# Revit family: RN 22120 Valvola inclinata
name_source: partatom
category: Rohrzubehör
units: mm (PartAtom-declared; Revit-internal decimal feet)

## family parameters
Arbeitsebenenbasiert = Nein
Beim Laden mit Abzugskörper schneiden = Nein
Bemaßung runder Anschluss = Durchmesser verwenden
Gemeinsam genutzt = Nein
Immer vertikal = Ja
Teiletyp = Ventil - Zerlegung in

## types (7) — shared parameters
1.010.00.2 Blattnummer der Richtlinie = 17
1.010.00.3 Ausgabedatum (Monat) der Richtlinie = 201601
1.010.00.4 Herstellername = R. Nussbaum AG
1.010.00.5 Revisionsdatum der Datei = 20190528
1.010.00.6 Webadresse des Herstellers = http://www.nussbaum.ch
1.100.00.3 Sortiernummer für Anzeigereihenfolge = 1
1.100.00.4 Produktbezeichnung = Absperrarmaturen
1.960/3L.00.8 Link (URL) = https://www.nussbaum.ch
17.700.00.4 Armaturentyp = 1
17.700.00.7 Maximale Betriebstemperatur TB [°C] = 90
17.700.00.8 Maximaler Betriebsdruck (Arbeitsdruck) ps [1.0 · 105 Pa] = 16
Connector Visibility = Nein
EnclosingSpace Visibility = Nein
Hersteller = R. Nussbauzm AG
URL = https://www.nussbaum.ch

## per-type parameters (varying)
- DN 25: 1.800.00.3 TGA-Nummer=001059???00000000000000000000200700000000000000001???00000; 1.810.00.3 Hersteller-Bestellnummer=22120.23; 1.810.00.4 DATANORM-Nummer=22120.23; 1.810.00.5 StLB-Nummer=727.113; 1.810.00.6 GTIN-Nummer=7612945733429; 17.700.00.30 Produktbeschreibung=22120.23, Schrägsitzventil, mit Flanschen, DN=25; 17.700.00.5 Nennweite DN=25; 17.700.00.6 kvs-Wert [m3/h]=22.14; CONNECTOR0_DIAMETER_dX_0r=25 mm  [stored 0.082021 ft]; CONNECTOR0_dX_00=81 mm; CONNECTOR0_dX_01=80 mm; CONNECTOR0_ref_dX=81 mm; CONNECTOR1_DIAMETER_dX_0r=25 mm  [stored 0.082021 ft]; CONNECTOR1_dX_00=80 mm; CONNECTOR1_dX_01=81 mm; CONNECTOR1_ref_dX=81 mm; Modell=22120.23; R. Nussbaum AG 22120.23 de Visibility=Ja; R. Nussbaum AG 22120.24 de Visibility=Nein; R. Nussbaum AG 22120.25 de Visibility=Nein; R. Nussbaum AG 22120.26 de Visibility=Nein; R. Nussbaum AG 22120.27 de Visibility=Nein; R. Nussbaum AG 22120.28 de Visibility=Nein; R. Nussbaum AG 22120.29 de Visibility=Nein; Typenkommentare=Valvola inclinataDN 25
- DN 32: 1.800.00.3 TGA-Nummer=001059???00000000000000000000200700000000000000002???00000; 1.810.00.3 Hersteller-Bestellnummer=22120.24; 1.810.00.4 DATANORM-Nummer=22120.24; 1.810.00.5 StLB-Nummer=727.114; 1.810.00.6 GTIN-Nummer=7612945733436; 17.700.00.30 Produktbeschreibung=22120.24, Schrägsitzventil, mit Flanschen, DN=32; 17.700.00.5 Nennweite DN=32; 17.700.00.6 kvs-Wert [m3/h]=37.32; CONNECTOR0_DIAMETER_dX_0r=32 mm; CONNECTOR0_dX_00=91 mm; CONNECTOR0_dX_01=90 mm; CONNECTOR0_ref_dX=91 mm; CONNECTOR1_DIAMETER_dX_0r=32 mm; CONNECTOR1_dX_00=90 mm; CONNECTOR1_dX_01=91 mm; CONNECTOR1_ref_dX=91 mm; Modell=22120.24; R. Nussbaum AG 22120.23 de Visibility=Nein; R. Nussbaum AG 22120.24 de Visibility=Ja; R. Nussbaum AG 22120.25 de Visibility=Nein; R. Nussbaum AG 22120.26 de Visibility=Nein; R. Nussbaum AG 22120.27 de Visibility=Nein; R. Nussbaum AG 22120.28 de Visibility=Nein; R. Nussbaum AG 22120.29 de Visibility=Nein; Typenkommentare=Valvola inclinataDN 32
- DN 40: 1.800.00.3 TGA-Nummer=001059???00000000000000000000200700000000000000003???00000; 1.810.00.3 Hersteller-Bestellnummer=22120.25; 1.810.00.4 DATANORM-Nummer=22120.25; 1.810.00.5 StLB-Nummer=727.115; 1.810.00.6 GTIN-Nummer=7612945733443; 17.700.00.30 Produktbeschreibung=22120.25, Schrägsitzventil, mit Flanschen, DN=40; 17.700.00.5 Nennweite DN=40; 17.700.00.6 kvs-Wert [m3/h]=51.4; CONNECTOR0_DIAMETER_dX_0r=40 mm; CONNECTOR0_dX_00=101 mm; CONNECTOR0_dX_01=100 mm  [stored 0.328084 ft]; CONNECTOR0_ref_dX=101 mm; CONNECTOR1_DIAMETER_dX_0r=40 mm; CONNECTOR1_dX_00=100 mm  [stored 0.328084 ft]; CONNECTOR1_dX_01=101 mm; CONNECTOR1_ref_dX=101 mm; Modell=22120.25; R. Nussbaum AG 22120.23 de Visibility=Nein; R. Nussbaum AG 22120.24 de Visibility=Nein; R. Nussbaum AG 22120.25 de Visibility=Ja; R. Nussbaum AG 22120.26 de Visibility=Nein; R. Nussbaum AG 22120.27 de Visibility=Nein; R. Nussbaum AG 22120.28 de Visibility=Nein; R. Nussbaum AG 22120.29 de Visibility=Nein; Typenkommentare=Valvola inclinataDN 40
- DN 50: 1.800.00.3 TGA-Nummer=001059???00000000000000000000200700000000000000004???00000; 1.810.00.3 Hersteller-Bestellnummer=22120.26; 1.810.00.4 DATANORM-Nummer=22120.26; 1.810.00.5 StLB-Nummer=727.116; 1.810.00.6 GTIN-Nummer=7612945733450; 17.700.00.30 Produktbeschreibung=22120.26, Schrägsitzventil, mit Flanschen, DN=50; 17.700.00.5 Nennweite DN=50; 17.700.00.6 kvs-Wert [m3/h]=89.64; CONNECTOR0_DIAMETER_dX_0r=50 mm; CONNECTOR0_dX_00=116 mm; CONNECTOR0_dX_01=115 mm; CONNECTOR0_ref_dX=116 mm; CONNECTOR1_DIAMETER_dX_0r=50 mm; CONNECTOR1_dX_00=115 mm; CONNECTOR1_dX_01=116 mm; CONNECTOR1_ref_dX=116 mm; Modell=22120.26; R. Nussbaum AG 22120.23 de Visibility=Nein; R. Nussbaum AG 22120.24 de Visibility=Nein; R. Nussbaum AG 22120.25 de Visibility=Nein; R. Nussbaum AG 22120.26 de Visibility=Ja; R. Nussbaum AG 22120.27 de Visibility=Nein; R. Nussbaum AG 22120.28 de Visibility=Nein; R. Nussbaum AG 22120.29 de Visibility=Nein; Typenkommentare=Valvola inclinataDN 50
- DN 65: 1.800.00.3 TGA-Nummer=001059???00000000000000000000200700000000000000005???00000; 1.810.00.3 Hersteller-Bestellnummer=22120.27; 1.810.00.4 DATANORM-Nummer=22120.27; 1.810.00.5 StLB-Nummer=727.117; 1.810.00.6 GTIN-Nummer=7612945726087; 17.700.00.30 Produktbeschreibung=22120.27, Schrägsitzventil, mit Flanschen, DN=65; 17.700.00.5 Nennweite DN=65; 17.700.00.6 kvs-Wert [m3/h]=137.04; CONNECTOR0_DIAMETER_dX_0r=65 mm; CONNECTOR0_dX_00=146 mm; CONNECTOR0_dX_01=145 mm; CONNECTOR0_ref_dX=146 mm; CONNECTOR1_DIAMETER_dX_0r=65 mm; CONNECTOR1_dX_00=145 mm; CONNECTOR1_dX_01=146 mm; CONNECTOR1_ref_dX=146 mm; Modell=22120.27; R. Nussbaum AG 22120.23 de Visibility=Nein; R. Nussbaum AG 22120.24 de Visibility=Nein; R. Nussbaum AG 22120.25 de Visibility=Nein; R. Nussbaum AG 22120.26 de Visibility=Nein; R. Nussbaum AG 22120.27 de Visibility=Ja; R. Nussbaum AG 22120.28 de Visibility=Nein; R. Nussbaum AG 22120.29 de Visibility=Nein; Typenkommentare=Valvola inclinataDN 65
- DN 80: 1.800.00.3 TGA-Nummer=001059???00000000000000000000200700000000000000006???00000; 1.810.00.3 Hersteller-Bestellnummer=22120.28; 1.810.00.4 DATANORM-Nummer=22120.28; 1.810.00.5 StLB-Nummer=727.118; 1.810.00.6 GTIN-Nummer=7612945726162; 17.700.00.30 Produktbeschreibung=22120.28, Schrägsitzventil, mit Flanschen, DN=80; 17.700.00.5 Nennweite DN=80; 17.700.00.6 kvs-Wert [m3/h]=212.29; CONNECTOR0_DIAMETER_dX_0r=80 mm; CONNECTOR0_dX_00=156 mm; CONNECTOR0_dX_01=155 mm; CONNECTOR0_ref_dX=156 mm; CONNECTOR1_DIAMETER_dX_0r=80 mm; CONNECTOR1_dX_00=155 mm; CONNECTOR1_dX_01=156 mm; CONNECTOR1_ref_dX=156 mm; Modell=22120.28; R. Nussbaum AG 22120.23 de Visibility=Nein; R. Nussbaum AG 22120.24 de Visibility=Nein; R. Nussbaum AG 22120.25 de Visibility=Nein; R. Nussbaum AG 22120.26 de Visibility=Nein; R. Nussbaum AG 22120.27 de Visibility=Nein; R. Nussbaum AG 22120.28 de Visibility=Ja; R. Nussbaum AG 22120.29 de Visibility=Nein; Typenkommentare=Valvola inclinataDN 80
- DN 100: 1.800.00.3 TGA-Nummer=001059???00000000000000000000200700000000000000007???00000; 1.810.00.3 Hersteller-Bestellnummer=22120.29; 1.810.00.4 DATANORM-Nummer=22120.29; 1.810.00.5 StLB-Nummer=727.121; 1.810.00.6 GTIN-Nummer=7612945726179; 17.700.00.30 Produktbeschreibung=22120.29, Schrägsitzventil, mit Flanschen, DN=100; 17.700.00.5 Nennweite DN=100; 17.700.00.6 kvs-Wert [m3/h]=368.8; CONNECTOR0_DIAMETER_dX_0r=100 mm  [stored 0.328084 ft]; CONNECTOR0_dX_00=176 mm; CONNECTOR0_dX_01=175 mm; CONNECTOR0_ref_dX=176 mm; CONNECTOR1_DIAMETER_dX_0r=100 mm  [stored 0.328084 ft]; CONNECTOR1_dX_00=175 mm; CONNECTOR1_dX_01=176 mm; CONNECTOR1_ref_dX=176 mm; Modell=22120.29; R. Nussbaum AG 22120.23 de Visibility=Nein; R. Nussbaum AG 22120.24 de Visibility=Nein; R. Nussbaum AG 22120.25 de Visibility=Nein; R. Nussbaum AG 22120.26 de Visibility=Nein; R. Nussbaum AG 22120.27 de Visibility=Nein; R. Nussbaum AG 22120.28 de Visibility=Nein; R. Nussbaum AG 22120.29 de Visibility=Ja; Typenkommentare=Valvola inclinataDN 100

note: [stored X ft] marks values corroborated as IEEE doubles in the binary element streams (Revit-internal decimal feet)

## geometry (parser evidence)
native form markers: Sweep x1
no freeform markers — native parametric forms only
